# Revit family: 3D BIM Model HydroWELL Select 70 and 120
name_source: partatom
category: Generic Models
units: mm (PartAtom-declared; Revit-internal decimal feet)

## family parameters
Always vertical = No
Can host rebar = No
Cut with Voids When Loaded = No
Part Type = Normal
Room Calculation Point = No
Round Connector Dimension = Use Radius
Shared = No
Work Plane-Based = No

## types (2) — shared parameters
Body = Aluminum 1100-H14
Description = Ultra Violet Disinfection
Manufacturer = Hydrotec
URL = http://www.hydrotec.co.uk

## per-type parameters (varying)
| type | Discharge offset | E/2 | FLG | Flange Connection | Flow Rate | Mass | Model | R |
| Select 70 | 105 mm  [stored 0.344488 ft] | 75 mm | 125 mm  [stored 0.410105 ft] | 150 mm | 27.8 L/s | 100.00 kg | HydroPUR Select 70
HydroPUR Select 70 | 75 mm |
| Select 120 | 130 mm | 100 mm  [stored 0.328084 ft] | 150 mm | 200 mm | 36.9 L/s | 125.00 kg | HydroPUR Select 120
HydroPUR Select 120 | 100 mm  [stored 0.328084 ft] |

note: [stored X ft] marks values corroborated as IEEE doubles in the binary element streams (Revit-internal decimal feet)

## geometry (parser evidence)
native form markers: Blend x2, Sweep x17
no freeform markers — native parametric forms only
